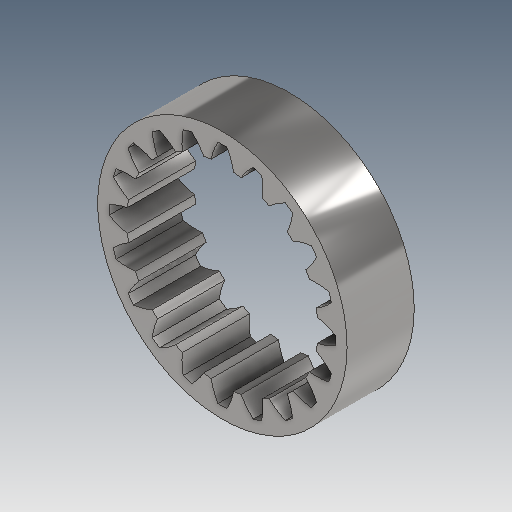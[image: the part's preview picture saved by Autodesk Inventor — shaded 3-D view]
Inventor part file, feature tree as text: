
AUTODESK INVENTOR PART (.ipt)
format: ipt  version: 2020.3 (Build 243373010, 373A)  size: 278,016 bytes
history: native  units: mm (DEFAULTED — no unit token found)
features: plane x3, other x3, sketch x2, extrude x1
ambient origin geometry x8: Origin, YZ Plane, XZ Plane, XY Plane, X Axis, Y Axis, Z Axis, Center Point
bodies: Solid1 (feature_tree)
feature tree (9):
  extrude  "Extrusion1"  Depth=10.0mm TaperAngle=0.0deg
  plane  "Work Plane2"
  plane  "Work Plane8"
  plane  "Work Plane9"
  other  "Spur Gear"
  sketch  "Sketch1"  dims[d0=37.125mm d1=10.0mm d2=0.0mm]
  sketch  "Sketch2"  dims[d3=30.0mm d4=10.0mm d5=0.0mm d16=6.0mm d17=0.0mm d34=1.570796mm d39=0.0mm d45=0.0mm d47=6.0mm d50=0.0mm d51=0.0mm d52=6.0mm]
  other  "Srf1"
  other  "Pitch Diameter"
